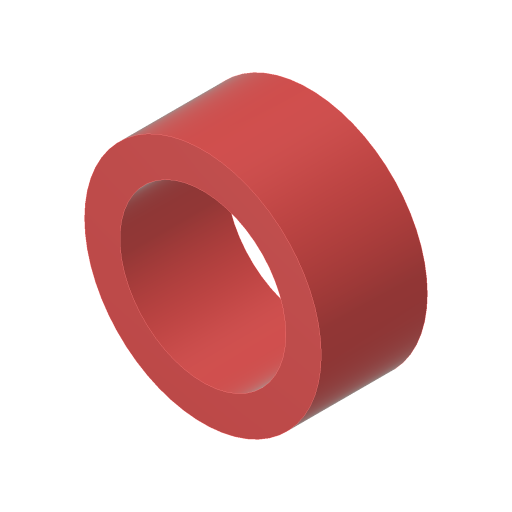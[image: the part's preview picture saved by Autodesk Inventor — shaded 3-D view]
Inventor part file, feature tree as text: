
AUTODESK INVENTOR PART (.ipt)
format: ipt  version: 2023.4 (Build 274418000, 418)  size: 114,688 bytes
history: native  units: in
note: dims shown in document units (in); Inventor stores cm internally (conversion verified against a paired STEP export)
features: extrude x1, sketch x1
ambient origin geometry x8: Origin, YZ Plane, XZ Plane, XY Plane, X Axis, Y Axis, Z Axis, Center Point
bodies: Solid1 (feature_tree)
feature tree (2):
  extrude  "Extrusion1"  Depth=0.3745in
  sketch  "Sketch1"  dims[d0=0.585in d1=0.125in d2=0.3745in d3=0.0in]
